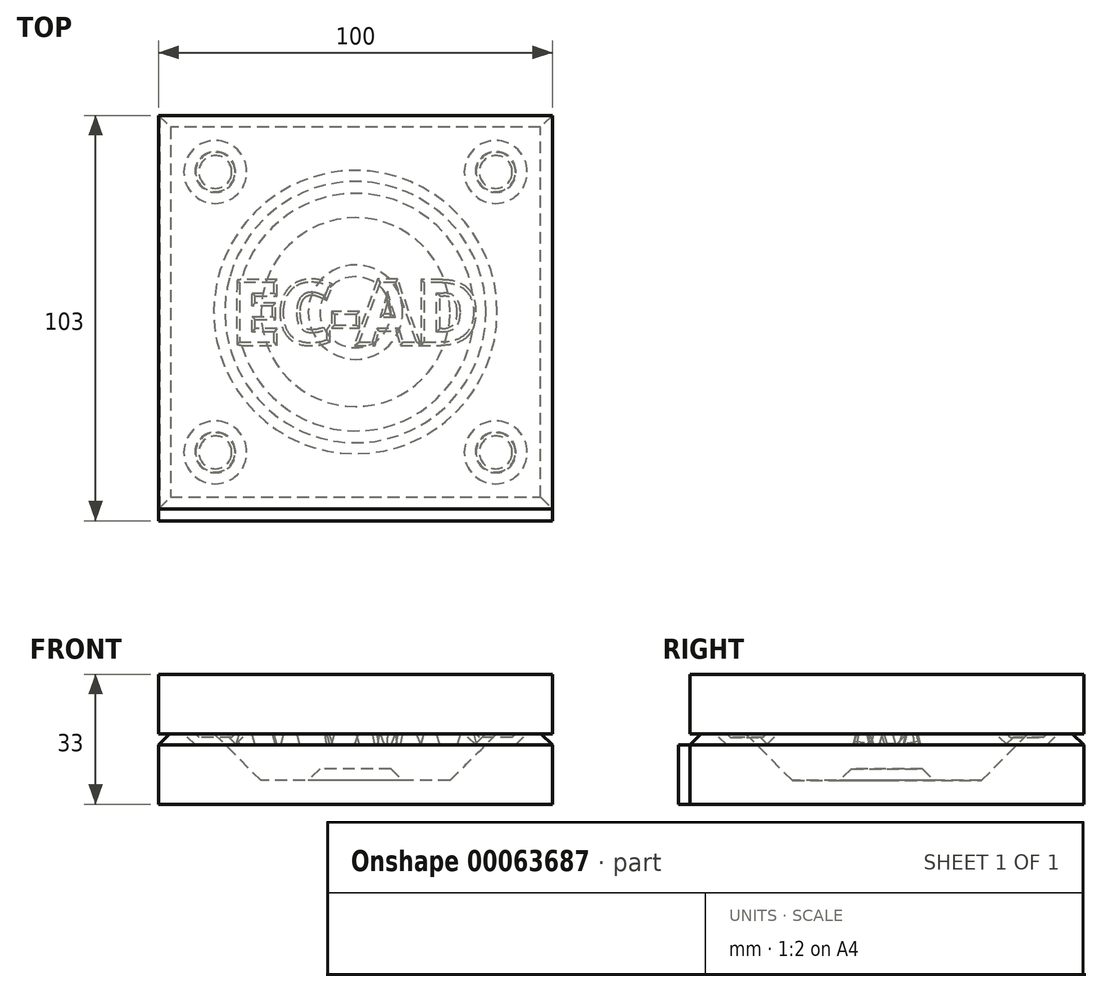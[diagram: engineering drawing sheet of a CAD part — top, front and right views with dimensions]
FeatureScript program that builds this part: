
annotation { "Feature Type Name" : "Feature", "Feature Type Description" : "" }
export const myFeature = defineFeature(function(context is Context, id is Id, definition is map)
    precondition{}
    {
        {
            var Q0;
            Q0=qCreatedBy(makeId("Top.planeOp"),FACE);
            var sketch = newSketch(context, id + "F0", { "sketchPlane" : qUnion([Q0])});
            skLineSegment(sketch, "E0.bottom", {"start": v(50, -50) * mm, "end": v(-50, -50) * mm});
            skLineSegment(sketch, "E0.top", {"start": v(50, 50) * mm, "end": v(-50, 50) * mm});
            skLineSegment(sketch, "E0.left", {"start": v(50, -50) * mm, "end": v(50, 50) * mm});
            skLineSegment(sketch, "E0.right", {"start": v(-50, -50) * mm, "end": v(-50, 50) * mm});
            skPoint(sketch, "E0.middle", {"position": v(0, 0) * mm});
            skSolve(sketch);
        }
        {
            var Q0;
            Q0 = qSketchRegion(id + "F0", true);
            extrude(context, id + "F1", {"entities" : qUnion([Q0]), "oppositeDirection" : true, "depth" : 18 * mm});
        }
        {
            var Q0;
            Q0=makeQuery(id+"F1.opExtrude","CAP_FACE",FACE,{"disambiguationData":[OSD([sQuery(id+"F0.wireOp",EDGE,"E0.bottom"),sQuery(id+"F0.wireOp",EDGE,"E0.top"),sQuery(id+"F0.wireOp",EDGE,"E0.left"),sQuery(id+"F0.wireOp",EDGE,"E0.right")])],"isStart":true});
            var sketch = newSketch(context, id + "F2", { "sketchPlane" : qUnion([Q0])});
            skCircle(sketch, "E1", {"center": v(0, 0) * mm, "radius": 36 * mm});
            skSolve(sketch);
        }
        {
            var Q0;
            Q0 = qSketchRegion(id + "F2", true);
            extrude(context, id + "F3", {"entities" : qUnion([Q0]), "operationType" : NewBodyOperationType.REMOVE, "oppositeDirection" : true, "depth" : 12 * mm, "hasDraft" : true, "draftAngle" : 45 * degree, "draftPullDirection" : true});
        }
        {
            var Q0;
            Q0=makeQuery(id+"F3.boolean.opBoolean","COPY",FACE,{"derivedFrom":makeQuery(id+"F3.opExtrude","CAP_FACE",FACE,{"disambiguationData":[OSD([sQuery(id+"F2.wireOp",EDGE,"E1")])],"isStart":false})});
            var sketch = newSketch(context, id + "F4", { "sketchPlane" : qUnion([Q0])});
            skCircle(sketch, "E2", {"center": v(0, 0) * mm, "radius": 12 * mm});
            skSolve(sketch);
        }
        {
            var Q0;
            Q0 = qSketchRegion(id + "F4", true);
            extrude(context, id + "F5", {"entities" : qUnion([Q0]), "operationType" : NewBodyOperationType.ADD, "depth" : 3 * mm, "hasDraft" : true, "draftAngle" : 45 * degree, "draftPullDirection" : true});
        }
        {
            var Q0;
            Q0=makeQuery(id+"F1.opExtrude","CAP_FACE",FACE,{"disambiguationData":[OSD([sQuery(id+"F0.wireOp",EDGE,"E0.bottom"),sQuery(id+"F0.wireOp",EDGE,"E0.top"),sQuery(id+"F0.wireOp",EDGE,"E0.left"),sQuery(id+"F0.wireOp",EDGE,"E0.right")])],"isStart":true});
            var sketch = newSketch(context, id + "F6", { "sketchPlane" : qUnion([Q0])});
            skLineSegment(sketch, "E3", {"start": v(-50, 35.62) * mm, "end": v(-35.62, 35.62) * mm, "construction": true});
            skLineSegment(sketch, "E4", {"start": v(-35.62, 35.62) * mm, "end": v(-25.36, 25.55) * mm, "construction": true});
            skLineSegment(sketch, "E5", {"start": v(-35.62, 35.62) * mm, "end": v(-35.62, 50) * mm, "construction": true});
            skCircle(sketch, "E6", {"center": v(-35.62, 35.62) * mm, "radius": 8 * mm});
            skCircle(sketch, "E7.1.0", {"center": v(-35.62, -35.62) * mm, "radius": 8 * mm});
            skCircle(sketch, "E7.2.0", {"center": v(35.62, -35.62) * mm, "radius": 8 * mm});
            skCircle(sketch, "E7.3.0", {"center": v(35.62, 35.62) * mm, "radius": 8 * mm});
            skPoint(sketch, "E7.center", {"position": v(0, 0) * mm});
            skSolve(sketch);
        }
        {
            var Q0;
            Q0=makeQuery(id+"F6.imprint","IMPRINT",FACE,{"disambiguationData":[TD([[makeQuery(id+"F6.imprint","IMPRINT",EDGE,{"derivedFrom":sQuery(id+"F6.wireOp",EDGE,"E6")}),1.0]])]});
            var Q1;
            Q1=makeQuery(id+"F6.imprint","IMPRINT",FACE,{"disambiguationData":[TD([[makeQuery(id+"F6.imprint","IMPRINT",EDGE,{"derivedFrom":sQuery(id+"F6.wireOp",EDGE,"E7.1.0")}),1.0]])]});
            var Q2;
            Q2=makeQuery(id+"F6.imprint","IMPRINT",FACE,{"disambiguationData":[TD([[makeQuery(id+"F6.imprint","IMPRINT",EDGE,{"derivedFrom":sQuery(id+"F6.wireOp",EDGE,"E7.3.0")}),1.0]])]});
            var Q3;
            Q3=makeQuery(id+"F6.imprint","IMPRINT",FACE,{"disambiguationData":[TD([[makeQuery(id+"F6.imprint","IMPRINT",EDGE,{"derivedFrom":sQuery(id+"F6.wireOp",EDGE,"E7.2.0")}),1.0]])]});
            extrude(context, id + "F7", {"entities" : qUnion([Q0, Q1, Q2, Q3]), "operationType" : NewBodyOperationType.REMOVE, "oppositeDirection" : true, "depth" : 3 * mm, "hasDraft" : true, "draftAngle" : 45 * degree, "draftPullDirection" : true});
        }
        {
            var Q0;
            Q0=makeQuery(id+"F1.opExtrude","CAP_EDGE",EDGE,{"disambiguationData":[OSD([sQuery(id+"F0.wireOp",EDGE,"E0.right")])],"isStart":true});
            var Q1;
            Q1=makeQuery(id+"F1.opExtrude","CAP_EDGE",EDGE,{"disambiguationData":[OSD([sQuery(id+"F0.wireOp",EDGE,"E0.bottom")])],"isStart":true});
            var Q2;
            Q2=makeQuery(id+"F1.opExtrude","CAP_EDGE",EDGE,{"disambiguationData":[OSD([sQuery(id+"F0.wireOp",EDGE,"E0.left")])],"isStart":true});
            var Q3;
            Q3=makeQuery(id+"F1.opExtrude","CAP_EDGE",EDGE,{"disambiguationData":[OSD([sQuery(id+"F0.wireOp",EDGE,"E0.top")])],"isStart":true});
            chamfer(context, id + "F8", {"entities" : qUnion([Q0, Q1, Q2, Q3]), "width" : 3 * mm, "tangentPropagation" : true});
        }
        {
            var Q0;
            Q0=makeQuery(id+"F1.opExtrude","CAP_FACE",FACE,{"disambiguationData":[OSD([sQuery(id+"F0.wireOp",EDGE,"E0.bottom"),sQuery(id+"F0.wireOp",EDGE,"E0.top"),sQuery(id+"F0.wireOp",EDGE,"E0.left"),sQuery(id+"F0.wireOp",EDGE,"E0.right")])],"isStart":true});
            var sketch = newSketch(context, id + "F9", { "sketchPlane" : qUnion([Q0])});
            skLineSegment(sketch, "E8.bottom", {"start": v(50, -50) * mm, "end": v(-50, -50) * mm});
            skLineSegment(sketch, "E8.top", {"start": v(50, 50) * mm, "end": v(-50, 50) * mm});
            skLineSegment(sketch, "E8.left", {"start": v(50, -50) * mm, "end": v(50, 50) * mm});
            skLineSegment(sketch, "E8.right", {"start": v(-50, -50) * mm, "end": v(-50, 50) * mm});
            skPoint(sketch, "E8.middle", {"position": v(0, 0) * mm});
            skSolve(sketch);
        }
        {
            var Q0;
            Q0 = qSketchRegion(id + "F9", true);
            extrude(context, id + "F10", {"entities" : qUnion([Q0]), "depth" : 15 * mm, "hasSecondDirection" : true, "secondDirectionOppositeDirection" : true, "secondDirectionDepth" : 3 * mm});
        }
        {
            var Q0;
            Q0=makeQuery(id+"F1.opExtrude","SWEPT_BODY",BODY,{"disambiguationData":[OSD([sQuery(id+"F0.wireOp",EDGE,"E0.bottom"),sQuery(id+"F0.wireOp",EDGE,"E0.top"),sQuery(id+"F0.wireOp",EDGE,"E0.left"),sQuery(id+"F0.wireOp",EDGE,"E0.right")])]});
            var Q1;
            Q1=makeQuery(id+"F10.opExtrude","SWEPT_BODY",BODY,{"disambiguationData":[OSD([sQuery(id+"F9.wireOp",EDGE,"E8.bottom"),sQuery(id+"F9.wireOp",EDGE,"E8.top"),sQuery(id+"F9.wireOp",EDGE,"E8.left"),sQuery(id+"F9.wireOp",EDGE,"E8.right")])]});
            var Q2;
            Q2=makeQuery(id+"F7.boolean.opBoolean","COPY",FACE,{"derivedFrom":makeQuery(id+"F7.opExtrude","SWEPT_FACE",FACE,{"disambiguationData":[OSD([sQuery(id+"F6.wireOp",EDGE,"E7.2.0")])]})});
            var Q3;
            Q3=makeQuery(id+"F7.boolean.opBoolean","COPY",FACE,{"derivedFrom":makeQuery(id+"F7.opExtrude","CAP_FACE",FACE,{"disambiguationData":[OSD([sQuery(id+"F6.wireOp",EDGE,"E7.2.0")])],"isStart":false})});
            var Q4;
            Q4=makeQuery(id+"F7.boolean.opBoolean","COPY",FACE,{"derivedFrom":makeQuery(id+"F7.opExtrude","CAP_FACE",FACE,{"disambiguationData":[OSD([sQuery(id+"F6.wireOp",EDGE,"E7.1.0")])],"isStart":false})});
            var Q5;
            Q5=makeQuery(id+"F7.boolean.opBoolean","COPY",FACE,{"derivedFrom":makeQuery(id+"F7.opExtrude","SWEPT_FACE",FACE,{"disambiguationData":[OSD([sQuery(id+"F6.wireOp",EDGE,"E7.1.0")])]})});
            var Q6;
            Q6=makeQuery(id+"F7.boolean.opBoolean","COPY",FACE,{"derivedFrom":makeQuery(id+"F7.opExtrude","CAP_FACE",FACE,{"disambiguationData":[OSD([sQuery(id+"F6.wireOp",EDGE,"E6")])],"isStart":false})});
            var Q7;
            Q7=makeQuery(id+"F7.boolean.opBoolean","COPY",FACE,{"derivedFrom":makeQuery(id+"F7.opExtrude","SWEPT_FACE",FACE,{"disambiguationData":[OSD([sQuery(id+"F6.wireOp",EDGE,"E6")])]})});
            var Q8;
            Q8=makeQuery(id+"F7.boolean.opBoolean","COPY",FACE,{"derivedFrom":makeQuery(id+"F7.opExtrude","CAP_FACE",FACE,{"disambiguationData":[OSD([sQuery(id+"F6.wireOp",EDGE,"E7.3.0")])],"isStart":false})});
            var Q9;
            Q9=makeQuery(id+"F7.boolean.opBoolean","COPY",FACE,{"derivedFrom":makeQuery(id+"F7.opExtrude","SWEPT_FACE",FACE,{"disambiguationData":[OSD([sQuery(id+"F6.wireOp",EDGE,"E7.3.0")])]})});
            var Q10;
            Q10=makeQuery(id+"F3.boolean.opBoolean","COPY",FACE,{"derivedFrom":makeQuery(id+"F3.opExtrude","SWEPT_FACE",FACE,{"disambiguationData":[OSD([sQuery(id+"F2.wireOp",EDGE,"E1")])]})});
            var Q11;
            Q11=makeQuery(id+"F8.opChamfer","BLEND_FACE",FACE,{"disambiguationData":[OSD([sQuery(id+"F0.wireOp",EDGE,"E0.bottom")])]});
            var Q12;
            Q12=makeQuery(id+"F8.opChamfer","BLEND_FACE",FACE,{"disambiguationData":[OSD([sQuery(id+"F0.wireOp",EDGE,"E0.right")])]});
            var Q13;
            Q13=makeQuery(id+"F8.opChamfer","BLEND_FACE",FACE,{"disambiguationData":[OSD([sQuery(id+"F0.wireOp",EDGE,"E0.top")])]});
            var Q14;
            Q14=makeQuery(id+"F8.opChamfer","BLEND_FACE",FACE,{"disambiguationData":[OSD([sQuery(id+"F0.wireOp",EDGE,"E0.left")])]});
            booleanBodies(context, id + "F11", {"operationType" : BooleanOperationType.SUBTRACTION, "tools" : qUnion([Q0]), "targets" : qUnion([Q1]), "offset" : true, "entitiesToOffset" : qUnion([Q2, Q3, Q4, Q5, Q6, Q7, Q8, Q9, Q10, Q11, Q12, Q13, Q14]), "offsetDistance" : 2 * mm, "keepTools" : true});
        }
        {
            var Q0;
            Q0=qCreatedBy(makeId("Top.planeOp"),FACE);
            var sketch = newSketch(context, id + "F12", { "sketchPlane" : qUnion([Q0])});
            skLineSegment(sketch, "E9.bottom", {"start": v(-29.31, 7.14) * mm, "end": v(29.31, 7.14) * mm, "construction": true});
            skLineSegment(sketch, "E9.top", {"start": v(-29.31, -7.14) * mm, "end": v(29.31, -7.14) * mm, "construction": true});
            skLineSegment(sketch, "E9.left", {"start": v(-29.31, 7.14) * mm, "end": v(-29.31, -7.14) * mm, "construction": true});
            skLineSegment(sketch, "E9.right", {"start": v(29.31, 7.14) * mm, "end": v(29.31, -7.14) * mm, "construction": true});
            skPoint(sketch, "E9.middle", {"position": v(0, 0) * mm});
            skText(sketch, "E10", { "text": "EC-AD", "fontName": "OpenSans-Bold.ttf"});
            const initialGuessF12  = {"E10": [-0.03138, -0.00764, 1, 0, 0.01528]};
            skSetInitialGuess(sketch, initialGuessF12);
            skSolve(sketch);
        }
        {
            var Q0;
            Q0 = qSketchRegion(id + "F12", true);
            extrude(context, id + "F13", {"entities" : qUnion([Q0]), "operationType" : NewBodyOperationType.REMOVE, "oppositeDirection" : true, "depth" : 3 * mm, "hasDraft" : true, "draftAngle" : 15 * degree});
        }
        {
            var Q0;
            Q0=makeQuery(id+"F1.opExtrude","SWEPT_FACE",FACE,{"disambiguationData":[OSD([sQuery(id+"F0.wireOp",EDGE,"E0.bottom")])]});
            var sketch = newSketch(context, id + "F14", { "sketchPlane" : qUnion([Q0])});
            skLineSegment(sketch, "E11.bottom", {"start": v(50, -18) * mm, "end": v(-50, -18) * mm});
            skLineSegment(sketch, "E11.top", {"start": v(50, -3) * mm, "end": v(-50, -3) * mm});
            skLineSegment(sketch, "E11.left", {"start": v(50, -18) * mm, "end": v(50, -3) * mm});
            skLineSegment(sketch, "E11.right", {"start": v(-50, -18) * mm, "end": v(-50, -3) * mm});
            skSolve(sketch);
        }
        {
            var Q0;
            Q0 = qSketchRegion(id + "F14", true);
            extrude(context, id + "F15", {"entities" : qUnion([Q0]), "depth" : 3 * mm});
        }
    });
